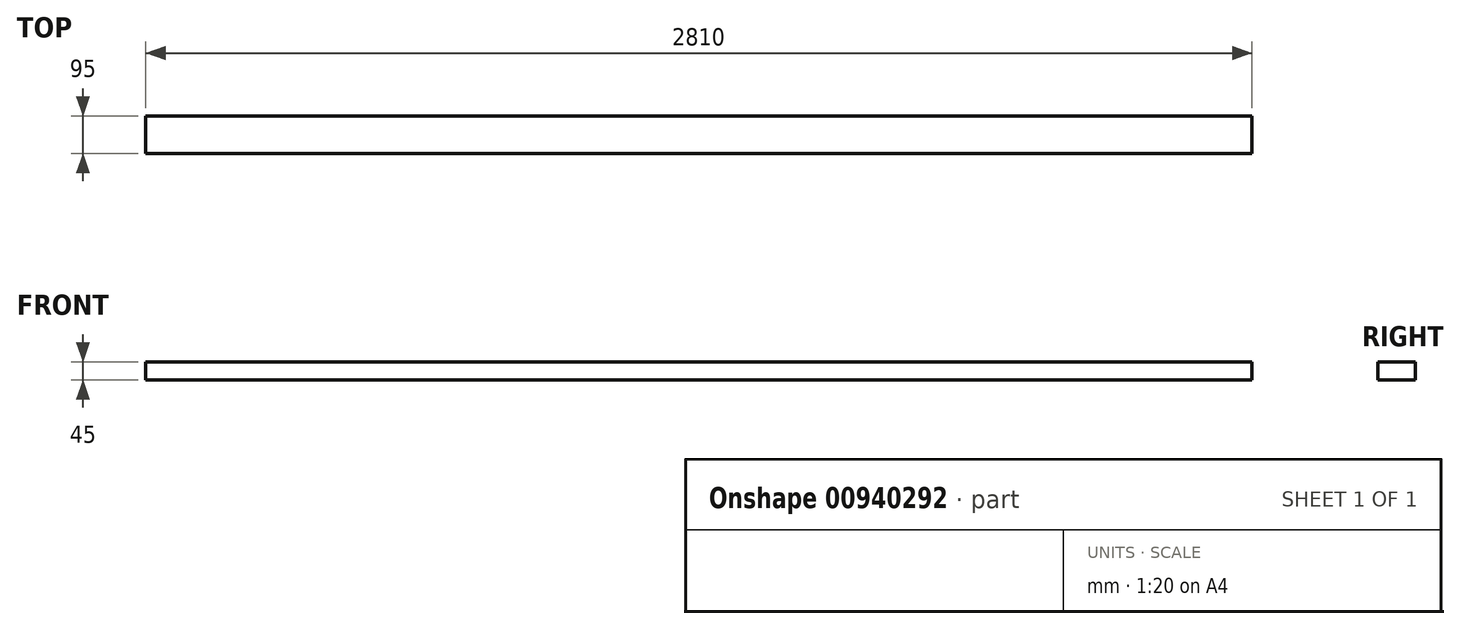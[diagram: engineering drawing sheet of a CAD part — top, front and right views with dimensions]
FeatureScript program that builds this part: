
annotation { "Feature Type Name" : "Feature", "Feature Type Description" : "" }
export const myFeature = defineFeature(function(context is Context, id is Id, definition is map)
    precondition{}
    {
        {
            var Q0;
            Q0=qCreatedBy(makeId("Right.planeOp"),FACE);
            var sketch = newSketch(context, id + "F0", { "sketchPlane" : qUnion([Q0])});
            skLineSegment(sketch, "E0.bottom", {"start": v(-47.5, 22.5) * mm, "end": v(47.5, 22.5) * mm});
            skLineSegment(sketch, "E0.top", {"start": v(-47.5, -22.5) * mm, "end": v(47.5, -22.5) * mm});
            skLineSegment(sketch, "E0.left", {"start": v(-47.5, 22.5) * mm, "end": v(-47.5, -22.5) * mm});
            skLineSegment(sketch, "E0.right", {"start": v(47.5, 22.5) * mm, "end": v(47.5, -22.5) * mm});
            skSolve(sketch);
        }
        {
            var Q0;
            Q0=qSketchRegion(id+"F0",true);
            extrude(context, id + "F1", {"entities" : qUnion([Q0]), "endBound" : BoundingType.SYMMETRIC, "depth" : 2810 * mm, "offsetDistance" : 25 * mm});
        }
    });
